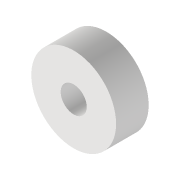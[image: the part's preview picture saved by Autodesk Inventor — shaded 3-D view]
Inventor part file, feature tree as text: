
AUTODESK INVENTOR PART (.ipt)
format: ipt  version: 2022.5 (Build 265521000, 521)  size: 93,696 bytes
history: native  units: mm
features: extrude x1, sketch x1
ambient origin geometry x8: Origin, YZ Plane, XZ Plane, XY Plane, X Axis, Y Axis, Z Axis, Center Point
bodies: Volumenkörper1 (feature_tree)
feature tree (2):
  extrude  "Extrusion1"  Depth=5.0mm
  sketch  "Skizze1"  dims[d0=4.0mm d1=13.0mm d2=5.0mm d3=0.0mm]
